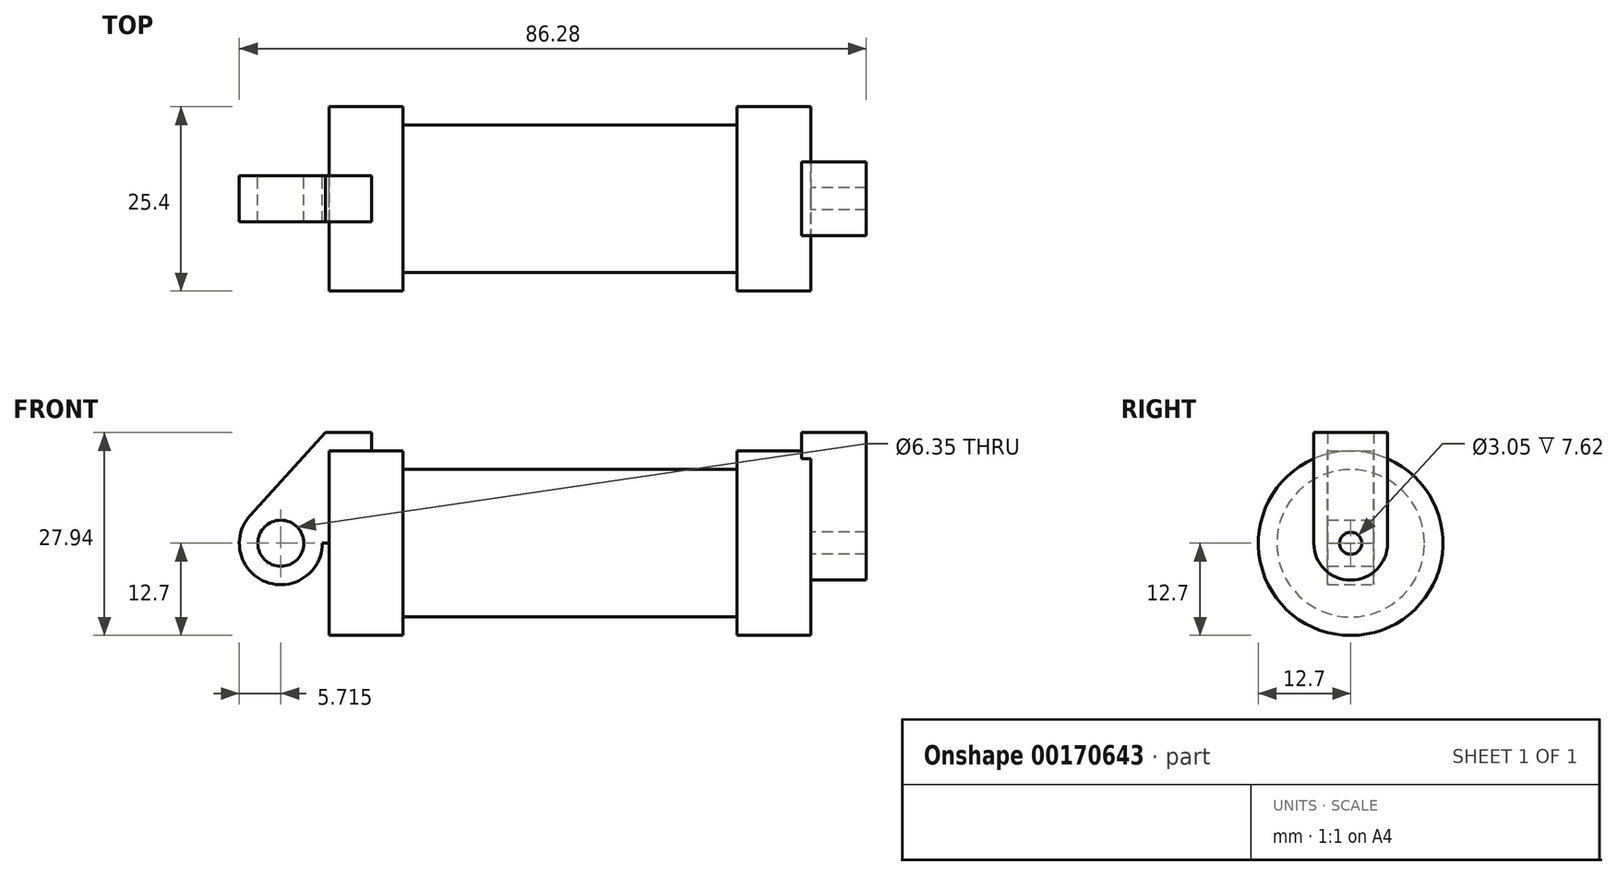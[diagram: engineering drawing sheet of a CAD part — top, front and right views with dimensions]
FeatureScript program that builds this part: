
annotation { "Feature Type Name" : "Feature", "Feature Type Description" : "" }
export const myFeature = defineFeature(function(context is Context, id is Id, definition is map)
    precondition{}
    {
        {
            var Q0;
            Q0=qCreatedBy(makeId("Front.planeOp"),FACE);
            var sketch = newSketch(context, id + "F0", { "sketchPlane" : qUnion([Q0])});
            skLineSegment(sketch, "E0", {"start": v(0, 0) * mm, "end": v(0, 12.7) * mm});
            skLineSegment(sketch, "E1", {"start": v(0, 12.7) * mm, "end": v(10.16, 12.7) * mm});
            skLineSegment(sketch, "E2", {"start": v(10.16, 12.7) * mm, "end": v(10.16, 10.16) * mm});
            skLineSegment(sketch, "E3", {"start": v(10.16, 10.16) * mm, "end": v(56.13, 10.16) * mm});
            skLineSegment(sketch, "E4", {"start": v(56.13, 10.16) * mm, "end": v(56.13, 12.7) * mm});
            skLineSegment(sketch, "E5", {"start": v(56.13, 12.7) * mm, "end": v(66.3, 12.7) * mm});
            skLineSegment(sketch, "E6", {"start": v(66.3, 12.7) * mm, "end": v(66.3, 0) * mm});
            skLineSegment(sketch, "E7", {"start": v(66.3, 0) * mm, "end": v(0, 0) * mm});
            skLineSegment(sketch, "E8", {"start": v(5.84, 15.24) * mm, "end": v(-0.5, 15.24) * mm});
            skLineSegment(sketch, "E9", {"start": v(-0.5, 15.24) * mm, "end": v(-10.88, 3.85) * mm});
            skLineSegment(sketch, "E10", {"start": v(0, 0) * mm, "end": v(-6.65, 0) * mm});
            skCircle(sketch, "E11", {"center": v(-6.65, 0) * mm, "radius": 5.72 * mm});
            skCircle(sketch, "E12", {"center": v(-6.65, 0) * mm, "radius": 3.18 * mm});
            skLineSegment(sketch, "E13", {"start": v(5.84, 15.24) * mm, "end": v(5.84, -9.4) * mm});
            skLineSegment(sketch, "E14", {"start": v(5.84, -9.4) * mm, "end": v(-8.18, -5.5) * mm});
            skSolve(sketch);
        }
        {
            var Q0;
            {var subQ0=sQuery(id+"F0.wireOp",EDGE,"E2");Q0=makeQuery(id+"F0.imprint","IMPRINT",FACE,{"disambiguationData":[TD([[makeQuery(id+"F0.imprint","IMPRINT",EDGE,{"derivedFrom":subQ0}),-1.0]])]});}
            var Q1;
            {var subQ0=sQuery(id+"F0.wireOp",EDGE,"E0");Q1=makeQuery(id+"F0.imprint","IMPRINT",FACE,{"disambiguationData":[TD([[makeQuery(id+"F0.imprint","IMPRINT",EDGE,{"derivedFrom":subQ0}),-1.0]])]});}
            var Q2;
            Q2=sQuery(id+"F0.wireOp",EDGE,"E7");
            revolve(context, id + "F1", {"entities" : qUnion([Q0, Q1]), "axis" : qUnion([Q2]), "revolveType" : RevolveType.FULL});
        }
        {
            var Q0;
            {var subQ3=sQuery(id+"F0.wireOp",EDGE,"E0");Q0=makeQuery(id+"F0.imprint","IMPRINT",FACE,{"disambiguationData":[TD([[makeQuery(id+"F0.imprint","IMPRINT",EDGE,{"derivedFrom":subQ3}),1.0]])]});}
            var Q1;
            {var subQ4=sQuery(id+"F0.wireOp",EDGE,"E12");Q1=makeQuery(id+"F0.imprint","IMPRINT",FACE,{"disambiguationData":[TD([[makeQuery(id+"F0.imprint","IMPRINT",EDGE,{"derivedFrom":subQ4}),-1.0]])]});}
            extrude(context, id + "F2", {"entities" : qUnion([Q0, Q1]), "endBound" : BoundingType.SYMMETRIC, "depth" : 6.35 * mm});
        }
        {
            var Q0;
            Q0=makeQuery(id+"F1.opRevolve","SWEPT_FACE",FACE,{"disambiguationData":[OSD([sQuery(id+"F0.wireOp",EDGE,"E6")])]});
            var sketch = newSketch(context, id + "F3", { "sketchPlane" : qUnion([Q0])});
            skCircle(sketch, "E15", {"center": v(0, 0) * mm, "radius": 5.08 * mm});
            skCircle(sketch, "E16", {"center": v(0, 0) * mm, "radius": 1.52 * mm});
            skLineSegment(sketch, "E17", {"start": v(-5.08, 0) * mm, "end": v(-5.08, 15.24) * mm});
            skLineSegment(sketch, "E18", {"start": v(5.08, 0) * mm, "end": v(5.08, 15.24) * mm});
            skLineSegment(sketch, "E19", {"start": v(5.08, 15.24) * mm, "end": v(-5.08, 15.24) * mm});
            skSolve(sketch);
        }
        {
            var Q0;
            {var subQ0=sQuery(id+"F3.wireOp",EDGE,"E17");var subQ1=sQuery(id+"F3.wireOp",EDGE,"E15");var subQ2=makeQuery(id+"F3.imprint","INTERSECT",VERTEX,{"derivedFrom":[subQ1,subQ0]});Q0=makeQuery(id+"F3.imprint","IMPRINT",FACE,{"disambiguationData":[TD([[makeQuery(id+"F3.imprint","IMPRINT",EDGE,{"disambiguationData":[TD([[subQ2,1.0]])],"derivedFrom":subQ1}),-1.0]])]});}
            var Q1;
            Q1=makeQuery(id+"F3.imprint","IMPRINT",FACE,{"disambiguationData":[TD([[makeQuery(id+"F3.imprint","IMPRINT",EDGE,{"derivedFrom":sQuery(id+"F3.wireOp",EDGE,"E16")}),-1.0]])]});
            var Q2;
            {var subQ0=sQuery(id+"F3.wireOp",EDGE,"E19");Q2=makeQuery(id+"F3.imprint","IMPRINT",FACE,{"disambiguationData":[TD([[makeQuery(id+"F3.imprint","IMPRINT",EDGE,{"derivedFrom":subQ0}),1.0]])]});}
            extrude(context, id + "F4", {"entities" : qUnion([Q0, Q1, Q2]), "operationType" : NewBodyOperationType.ADD, "depth" : 7.62 * mm, "hasSecondDirection" : true, "secondDirectionOppositeDirection" : true, "secondDirectionDepth" : 1.27 * mm});
        }
    });
